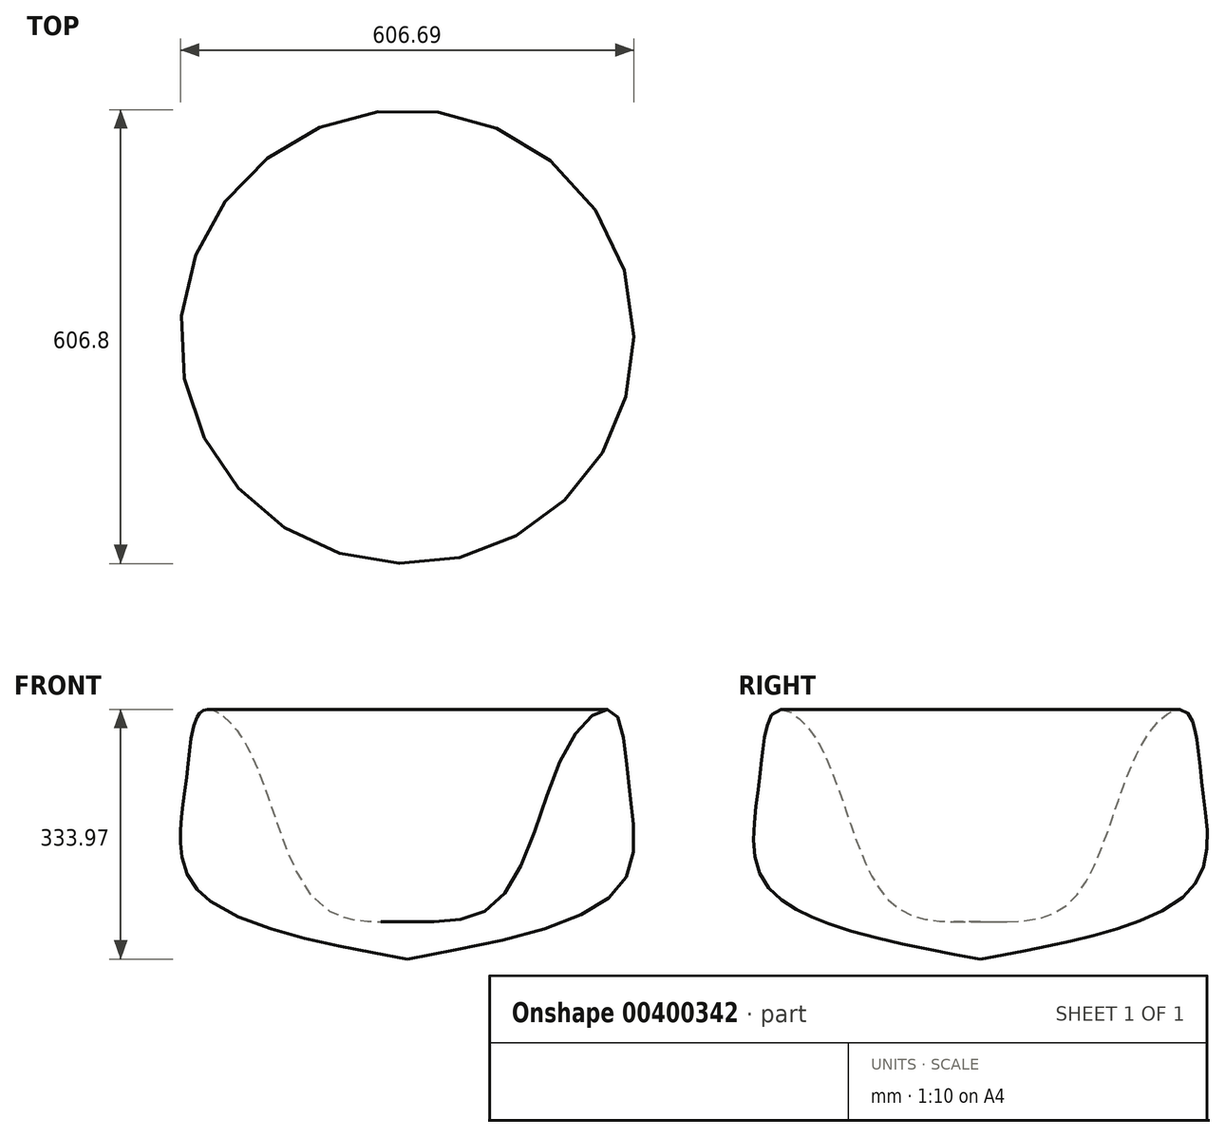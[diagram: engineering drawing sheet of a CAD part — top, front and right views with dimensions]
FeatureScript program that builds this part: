
annotation { "Feature Type Name" : "Feature", "Feature Type Description" : "" }
export const myFeature = defineFeature(function(context is Context, id is Id, definition is map)
    precondition{}
    {
        {
            var Q0;
            Q0=qCreatedBy(makeId("Front.planeOp"),FACE);
            var sketch = newSketch(context, id + "F0", { "sketchPlane" : qUnion([Q0])});
            skLineSegment(sketch, "E0", {"start": v(0, 118.49) * mm, "end": v(0, -137.78) * mm});
            skFitSpline(sketch, "E1", {"points": [v(0, -86.52) * mm, v(122.76, -59.17) * mm, v(215.66, 149.17) * mm, v(273.31, 194.64) * mm, v(295.74, 100.75) * mm, v(286.13, -38.7) * mm, v(0, -137.78) * mm], "startDerivative": vector(902.72, -46.56) * mm, "endDerivative": vector(-1569.5, -286.9) * mm});
            skSolve(sketch);
        }
        {
            var Q0;
            {var subQ0=sQuery(id+"F0.wireOp",EDGE,"E1");Q0=makeQuery(id+"F0.imprint","IMPRINT",FACE,{"disambiguationData":[TD([[makeQuery(id+"F0.imprint","IMPRINT",EDGE,{"derivedFrom":subQ0}),-1.0]])]});}
            var Q1;
            Q1=sQuery(id+"F0.wireOp",EDGE,"E0");
            revolve(context, id + "F1", {"entities" : qUnion([Q0]), "axis" : qUnion([Q1]), "revolveType" : RevolveType.FULL});
        }
    });
